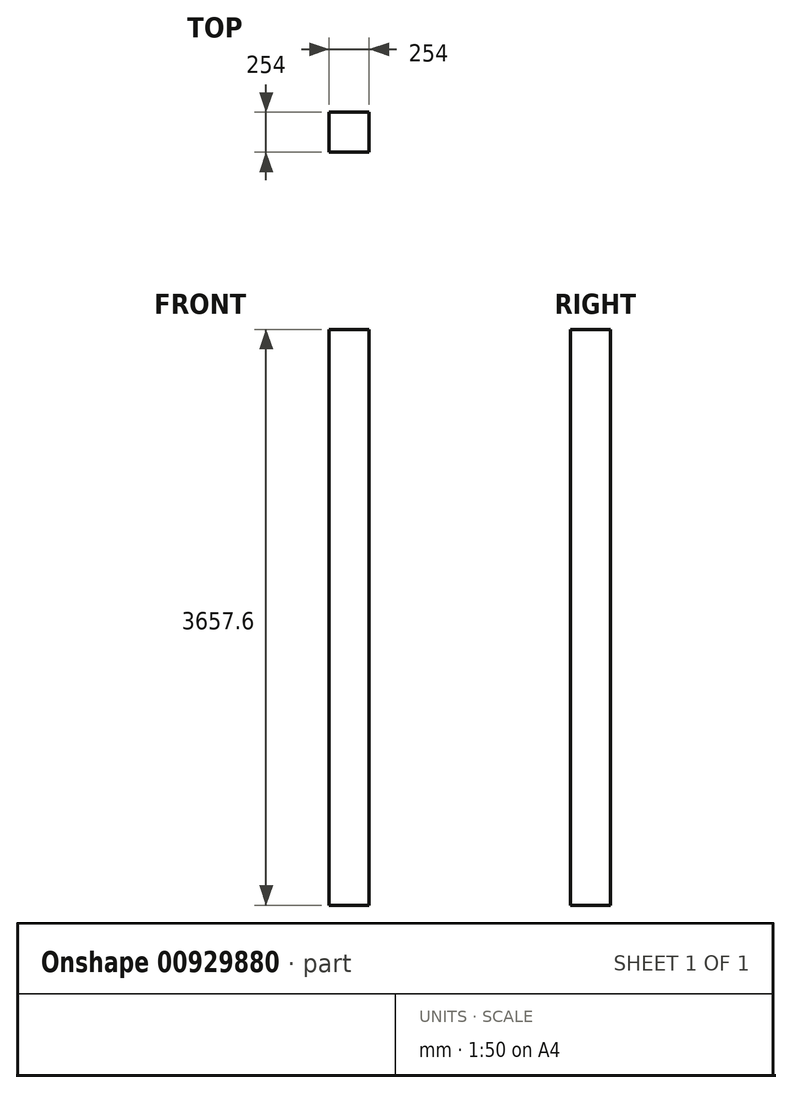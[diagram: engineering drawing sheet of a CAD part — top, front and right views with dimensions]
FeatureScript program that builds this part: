
annotation { "Feature Type Name" : "Feature", "Feature Type Description" : "" }
export const myFeature = defineFeature(function(context is Context, id is Id, definition is map)
    precondition{}
    {
        {
            var Q0;
            Q0=qCreatedBy(makeId("Top.planeOp"),FACE);
            var sketch = newSketch(context, id + "F0", { "sketchPlane" : qUnion([Q0])});
            skLineSegment(sketch, "E0.bottom", {"start": v(-203.31, -165.47) * mm, "end": v(50.69, -165.47) * mm});
            skLineSegment(sketch, "E0.top", {"start": v(-203.31, 88.53) * mm, "end": v(50.69, 88.53) * mm});
            skLineSegment(sketch, "E0.left", {"start": v(-203.31, -165.47) * mm, "end": v(-203.31, 88.53) * mm});
            skLineSegment(sketch, "E0.right", {"start": v(50.69, -165.47) * mm, "end": v(50.69, 88.53) * mm});
            skSolve(sketch);
        }
        {
            var Q0;
            Q0=makeQuery(id+"F0.imprint","IMPRINT",FACE,{"disambiguationData":[TD([[makeQuery(id+"F0.imprint","IMPRINT",EDGE,{"derivedFrom":sQuery(id+"F0.wireOp",EDGE,"E0.bottom")}),1.0]])]});
            extrude(context, id + "F1", {"entities" : qUnion([Q0]), "depth" : 3657.6 * mm, "offsetDistance" : 25.4 * mm});
        }
    });
